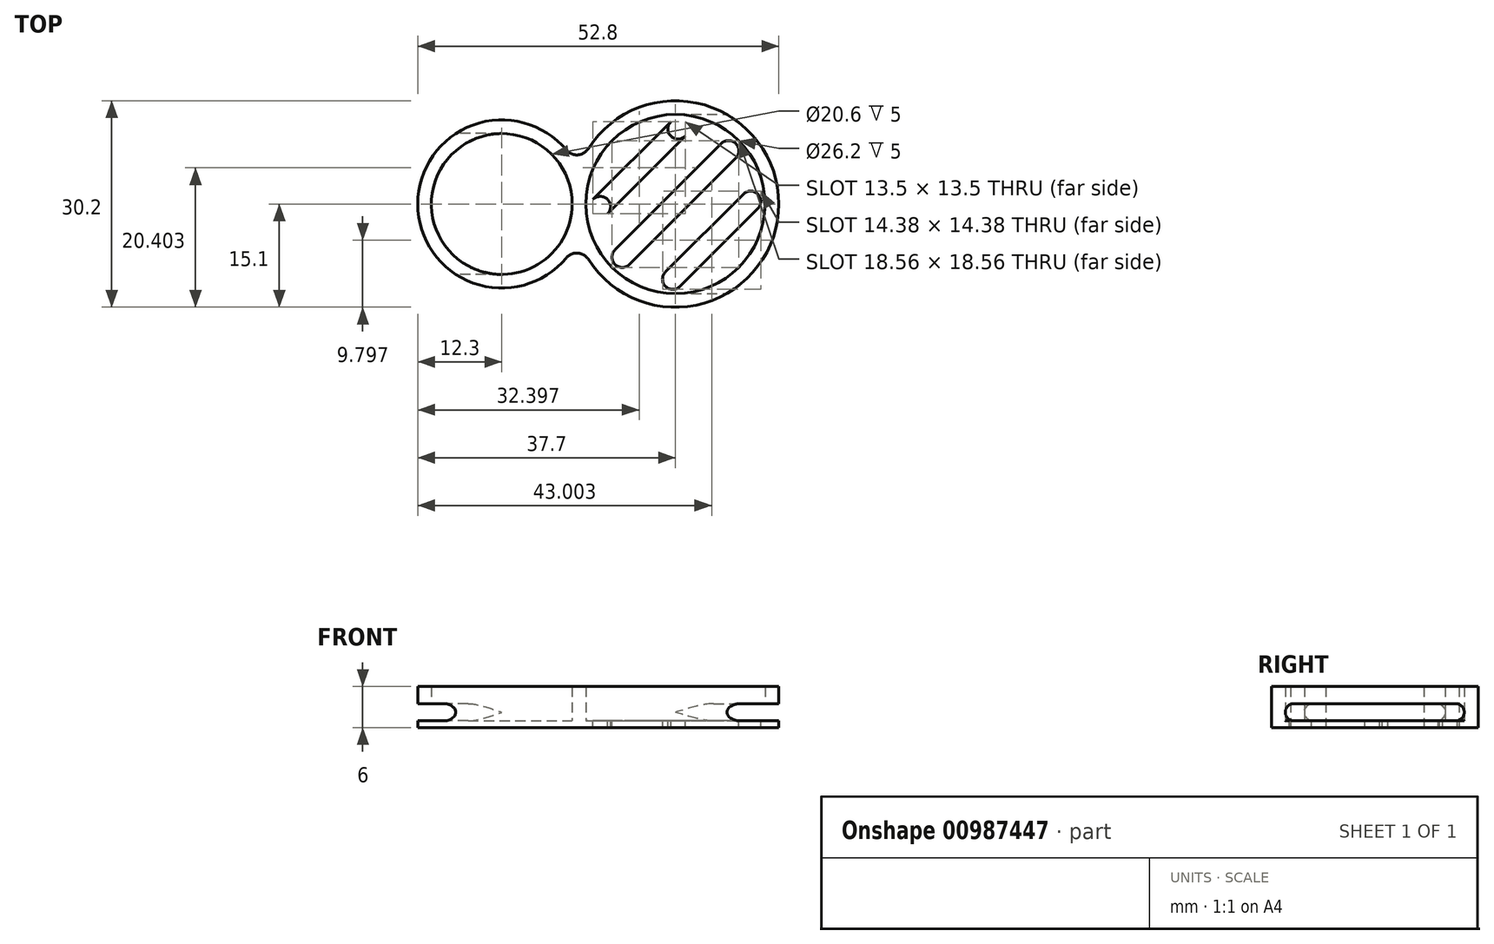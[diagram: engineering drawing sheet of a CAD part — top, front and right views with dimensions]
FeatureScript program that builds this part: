
annotation { "Feature Type Name" : "Feature", "Feature Type Description" : "" }
export const myFeature = defineFeature(function(context is Context, id is Id, definition is map)
    precondition{}
    {
        {
            var Q0;
            Q0=qCreatedBy(makeId("Top.planeOp"),FACE);
            var sketch = newSketch(context, id + "F0", { "sketchPlane" : qUnion([Q0])});
            skCircle(sketch, "E0", {"center": v(-11.3, 0) * mm, "radius": 10.3 * mm});
            skCircle(sketch, "E1", {"center": v(14.1, 0) * mm, "radius": 13.1 * mm});
            skArc(sketch, "E2", {"start": v(1.36, -8.1) * mm, "mid": v(29.2, 0) * mm, "end": v(1.36, 8.1) * mm});
            skArc(sketch, "E3", {"start": v(-1.86, 7.9) * mm, "mid": v(-23.6, 0) * mm, "end": v(-1.86, -7.9) * mm});
            skPoint(sketch, "E4.visualSharp", {"position": v(-0.11, -5.1) * mm});
            skArc(sketch, "E4.filletArc", {"start": v(1.36, -8.1) * mm, "mid": v(-0.2, -7.18) * mm, "end": v(-1.86, -7.9) * mm});
            skPoint(sketch, "E5.visualSharp", {"position": v(-0.11, 5.1) * mm});
            skArc(sketch, "E5.filletArc", {"start": v(-1.86, 7.9) * mm, "mid": v(-0.2, 7.18) * mm, "end": v(1.36, 8.1) * mm});
            skSolve(sketch);
        }
        {
            var Q0;
            Q0 = qSketchRegion(id + "F0", true);
            var Q1;
            Q1=makeQuery(id+"F0.imprint","IMPRINT",FACE,{"disambiguationData":[TD([[makeQuery(id+"F0.imprint","IMPRINT",EDGE,{"derivedFrom":sQuery(id+"F0.wireOp",EDGE,"E0")}),1.0]])]});
            var Q2;
            Q2=makeQuery(id+"F0.imprint","IMPRINT",FACE,{"disambiguationData":[TD([[makeQuery(id+"F0.imprint","IMPRINT",EDGE,{"derivedFrom":sQuery(id+"F0.wireOp",EDGE,"E1")}),1.0]])]});
            extrude(context, id + "F1", {"entities" : qUnion([Q0, Q1, Q2]), "depth" : 1 * mm, "offsetDistance" : 25 * mm});
        }
        {
            var Q0;
            Q0=makeQuery(id+"F0.imprint","IMPRINT",FACE,{"disambiguationData":[TD([[makeQuery(id+"F0.imprint","IMPRINT",EDGE,{"derivedFrom":sQuery(id+"F0.wireOp",EDGE,"E0")}),-1.0]])]});
            extrude(context, id + "F2", {"entities" : qUnion([Q0]), "operationType" : NewBodyOperationType.ADD, "depth" : 6 * mm, "offsetDistance" : 25 * mm});
        }
        {
            var Q0;
            Q0=qCreatedBy(makeId("Right.planeOp"),FACE);
            cPlane(context, id + "F3", {"entities" : qUnion([Q0]), "cplaneType" : CPlaneType.OFFSET, "offset" : 40 * mm, "oppositeDirection" : true, "width" : 150 * mm, "height" : 150 * mm});
        }
        {
            var Q0;
            Q0=qCreatedBy(id+"F3.planeOp",FACE);
            var sketch = newSketch(context, id + "F4", { "sketchPlane" : qUnion([Q0])});
            skLineSegment(sketch, "E6.bottom", {"start": v(9.05, 3.5) * mm, "end": v(-9.05, 3.5) * mm});
            skLineSegment(sketch, "E6.top", {"start": v(9.05, 1) * mm, "end": v(-9.05, 1) * mm});
            skLineSegment(sketch, "E6.left", {"start": v(10.3, 2.25) * mm, "end": v(10.3, 2.25) * mm});
            skLineSegment(sketch, "E6.right", {"start": v(-10.3, 2.25) * mm, "end": v(-10.3, 2.25) * mm});
            skLineSegment(sketch, "E7", {"start": v(0, 1) * mm, "end": v(0, 0) * mm, "construction": true});
            skPoint(sketch, "E8.visualSharp", {"position": v(10.3, 3.5) * mm});
            skArc(sketch, "E8.filletArc", {"start": v(10.3, 2.25) * mm, "mid": v(9.93, 3.13) * mm, "end": v(9.05, 3.5) * mm});
            skPoint(sketch, "E9.visualSharp", {"position": v(10.3, 1) * mm});
            skArc(sketch, "E9.filletArc", {"start": v(9.05, 1) * mm, "mid": v(9.93, 1.37) * mm, "end": v(10.3, 2.25) * mm});
            skPoint(sketch, "E10.visualSharp", {"position": v(-10.3, 1) * mm});
            skArc(sketch, "E10.filletArc", {"start": v(-10.3, 2.25) * mm, "mid": v(-9.93, 1.37) * mm, "end": v(-9.05, 1) * mm});
            skPoint(sketch, "E11.visualSharp", {"position": v(-10.3, 3.5) * mm});
            skArc(sketch, "E11.filletArc", {"start": v(-9.05, 3.5) * mm, "mid": v(-9.93, 3.13) * mm, "end": v(-10.3, 2.25) * mm});
            skSolve(sketch);
        }
        {
            var Q0;
            Q0 = qSketchRegion(id + "F4", true);
            extrude(context, id + "F5", {"entities" : qUnion([Q0]), "operationType" : NewBodyOperationType.REMOVE, "depth" : 28.7 * mm, "offsetDistance" : 25 * mm});
        }
        {
            var Q0;
            Q0=qCreatedBy(makeId("Right.planeOp"),FACE);
            cPlane(context, id + "F6", {"entities" : qUnion([Q0]), "cplaneType" : CPlaneType.OFFSET, "offset" : 40 * mm, "width" : 150 * mm, "height" : 150 * mm});
        }
        {
            var Q0;
            Q0=qCreatedBy(id+"F6.planeOp",FACE);
            var sketch = newSketch(context, id + "F7", { "sketchPlane" : qUnion([Q0])});
            skLineSegment(sketch, "E12.bottom", {"start": v(-11.85, 3.5) * mm, "end": v(11.85, 3.5) * mm});
            skLineSegment(sketch, "E12.top", {"start": v(-11.85, 1) * mm, "end": v(11.85, 1) * mm});
            skLineSegment(sketch, "E12.left", {"start": v(-13.1, 2.25) * mm, "end": v(-13.1, 2.25) * mm});
            skLineSegment(sketch, "E12.right", {"start": v(13.1, 2.25) * mm, "end": v(13.1, 2.25) * mm});
            skLineSegment(sketch, "E13", {"start": v(0, 1) * mm, "end": v(0, 0) * mm, "construction": true});
            skPoint(sketch, "E14.visualSharp", {"position": v(13.1, 1) * mm});
            skArc(sketch, "E14.filletArc", {"start": v(11.85, 1) * mm, "mid": v(12.73, 1.37) * mm, "end": v(13.1, 2.25) * mm});
            skPoint(sketch, "E15.visualSharp", {"position": v(13.1, 3.5) * mm});
            skArc(sketch, "E15.filletArc", {"start": v(13.1, 2.25) * mm, "mid": v(12.73, 3.13) * mm, "end": v(11.85, 3.5) * mm});
            skPoint(sketch, "E16.visualSharp", {"position": v(-13.1, 1) * mm});
            skArc(sketch, "E16.filletArc", {"start": v(-13.1, 2.25) * mm, "mid": v(-12.73, 1.37) * mm, "end": v(-11.85, 1) * mm});
            skPoint(sketch, "E17.visualSharp", {"position": v(-13.1, 3.5) * mm});
            skArc(sketch, "E17.filletArc", {"start": v(-11.85, 3.5) * mm, "mid": v(-12.73, 3.13) * mm, "end": v(-13.1, 2.25) * mm});
            skSolve(sketch);
        }
        {
            var Q0;
            Q0 = qSketchRegion(id + "F7", true);
            extrude(context, id + "F8", {"entities" : qUnion([Q0]), "operationType" : NewBodyOperationType.REMOVE, "oppositeDirection" : true, "depth" : 25.9 * mm, "offsetDistance" : 25 * mm});
        }
        {
            var Q0;
            Q0=makeQuery(id+"F8.boolean.opBoolean","MERGE",FACE,{"derivedFrom":[makeQuery(id+"F2.boolean.opBoolean","SPLIT",FACE,{"disambiguationData":[TD([makeQuery(id+"F2.opExtrude","SWEPT_FACE",FACE,{"disambiguationData":[OSD([sQuery(id+"F0.wireOp",EDGE,"E1")])]})])],"derivedFrom":makeQuery(id+"F1.opExtrude","CAP_FACE",FACE,{"disambiguationData":[OSD([sQuery(id+"F0.wireOp",EDGE,"E2"),sQuery(id+"F0.wireOp",EDGE,"E3"),sQuery(id+"F0.wireOp",EDGE,"E4.filletArc"),sQuery(id+"F0.wireOp",EDGE,"E5.filletArc")])],"isStart":false})})],"fromTools":[makeQuery(id+"F8.opExtrude","SWEPT_FACE",FACE,{"disambiguationData":[OSD([sQuery(id+"F7.wireOp",EDGE,"E12.top")])]})]});
            var sketch = newSketch(context, id + "F9", { "sketchPlane" : qUnion([Q0])});
            skCircle(sketch, "E18", {"center": v(14.1, 0) * mm, "radius": 12.5 * mm});
            skLineSegment(sketch, "E19", {"start": v(5.26, -8.84) * mm, "end": v(22.94, 8.84) * mm, "construction": true});
            skLineSegment(sketch, "E20", {"start": v(14.1, 12.5) * mm, "end": v(14.1, -12.5) * mm, "construction": true});
            skLineSegment(sketch, "E21", {"start": v(5.26, -6.72) * mm, "end": v(20.82, 8.84) * mm});
            skLineSegment(sketch, "E22", {"start": v(22.94, 8.84) * mm, "end": v(22.94, 8.84) * mm});
            skLineSegment(sketch, "E23", {"start": v(22.94, 6.72) * mm, "end": v(7.38, -8.84) * mm});
            skLineSegment(sketch, "E24", {"start": v(5.26, -8.84) * mm, "end": v(5.26, -8.84) * mm});
            skLineSegment(sketch, "E25", {"start": v(13.04, 1.06) * mm, "end": v(14.1, 0) * mm});
            skPoint(sketch, "E26.visualSharp", {"position": v(24, 7.78) * mm});
            skArc(sketch, "E26.filletArc", {"start": v(22.94, 6.72) * mm, "mid": v(23.38, 7.78) * mm, "end": v(22.94, 8.84) * mm});
            skPoint(sketch, "E27.visualSharp", {"position": v(21.88, 9.9) * mm});
            skArc(sketch, "E27.filletArc", {"start": v(22.94, 8.84) * mm, "mid": v(21.88, 9.28) * mm, "end": v(20.82, 8.84) * mm});
            skPoint(sketch, "E28.visualSharp", {"position": v(6.32, -9.9) * mm});
            skArc(sketch, "E28.filletArc", {"start": v(5.26, -8.84) * mm, "mid": v(6.32, -9.28) * mm, "end": v(7.38, -8.84) * mm});
            skPoint(sketch, "E29.visualSharp", {"position": v(4.2, -7.78) * mm});
            skArc(sketch, "E29.filletArc", {"start": v(5.26, -6.72) * mm, "mid": v(4.82, -7.78) * mm, "end": v(5.26, -8.84) * mm});
            skLineSegment(sketch, "E30", {"start": v(12.33, -12.37) * mm, "end": v(26.47, 1.77) * mm, "construction": true});
            skLineSegment(sketch, "E31", {"start": v(24.03, 1.45) * mm, "end": v(12.65, -9.93) * mm});
            skLineSegment(sketch, "E32", {"start": v(14.77, -12.05) * mm, "end": v(26.15, -0.67) * mm});
            skLineSegment(sketch, "E33", {"start": v(18.34, -4.24) * mm, "end": v(5.26, 8.84) * mm, "construction": true});
            skCircle(sketch, "E34", {"center": v(25.1, 0.39) * mm, "radius": 1.5 * mm});
            skCircle(sketch, "E35", {"center": v(13.71, -11) * mm, "radius": 1.5 * mm});
            skPoint(sketch, "E36.orphan", {"position": v(26.3, 3.71) * mm});
            skPoint(sketch, "E37.start.orphan", {"position": v(10.39, -12.2) * mm});
            skLineSegment(sketch, "E38.MirrorCS", {"start": v(15.55, 9.93) * mm, "end": v(4.17, -1.45) * mm});
            skCircle(sketch, "E39.MirrorC", {"center": v(3.1, -0.39) * mm, "radius": 1.5 * mm});
            skLineSegment(sketch, "E40.MirrorCS", {"start": v(2.05, 0.67) * mm, "end": v(13.43, 12.05) * mm});
            skCircle(sketch, "E41.MirrorC", {"center": v(14.49, 11) * mm, "radius": 1.5 * mm});
            skSolve(sketch);
        }
        {
            var Q0;
            {var subQ0=sQuery(id+"F9.wireOp",EDGE,"E38.MirrorCS");Q0=makeQuery(id+"F9.imprint","IMPRINT",FACE,{"disambiguationData":[TD([[makeQuery(id+"F9.imprint","IMPRINT",EDGE,{"derivedFrom":subQ0}),-1.0]])]});}
            var Q1;
            {var subQ0=sQuery(id+"F9.wireOp",EDGE,"E41.MirrorC");var subQ1=makeQuery(id+"F9.imprint","INTERSECT",VERTEX,{"derivedFrom":[sQuery(id+"F9.wireOp",EDGE,"E38.MirrorCS"),subQ0]});Q1=makeQuery(id+"F9.imprint","IMPRINT",FACE,{"disambiguationData":[TD([[makeQuery(id+"F9.imprint","IMPRINT",EDGE,{"disambiguationData":[TD([[subQ1,1.0]])],"derivedFrom":subQ0}),-1.0]])]});}
            var Q2;
            {var subQ0=sQuery(id+"F9.wireOp",EDGE,"E39.MirrorC");var subQ1=makeQuery(id+"F9.imprint","INTERSECT",VERTEX,{"derivedFrom":[sQuery(id+"F9.wireOp",EDGE,"E38.MirrorCS"),subQ0]});Q2=makeQuery(id+"F9.imprint","IMPRINT",FACE,{"disambiguationData":[TD([[makeQuery(id+"F9.imprint","IMPRINT",EDGE,{"disambiguationData":[TD([[subQ1,-1.0]])],"derivedFrom":subQ0}),-1.0]])]});}
            var Q3;
            Q3=makeQuery(id+"F9.imprint","IMPRINT",FACE,{"disambiguationData":[TD([[makeQuery(id+"F9.imprint","IMPRINT",EDGE,{"derivedFrom":sQuery(id+"F9.wireOp",EDGE,"E23")}),-1.0]])]});
            var Q4;
            {var subQ0=sQuery(id+"F9.wireOp",EDGE,"E31");Q4=makeQuery(id+"F9.imprint","IMPRINT",FACE,{"disambiguationData":[TD([[makeQuery(id+"F9.imprint","IMPRINT",EDGE,{"derivedFrom":subQ0}),1.0]])]});}
            var Q5;
            {var subQ0=sQuery(id+"F9.wireOp",EDGE,"E35");var subQ1=makeQuery(id+"F9.imprint","INTERSECT",VERTEX,{"derivedFrom":[sQuery(id+"F9.wireOp",EDGE,"E31"),subQ0]});Q5=makeQuery(id+"F9.imprint","IMPRINT",FACE,{"disambiguationData":[TD([[makeQuery(id+"F9.imprint","IMPRINT",EDGE,{"disambiguationData":[TD([[subQ1,-1.0]])],"derivedFrom":subQ0}),1.0]])]});}
            var Q6;
            {var subQ0=sQuery(id+"F9.wireOp",EDGE,"E34");var subQ1=makeQuery(id+"F9.imprint","INTERSECT",VERTEX,{"derivedFrom":[sQuery(id+"F9.wireOp",EDGE,"E31"),subQ0]});Q6=makeQuery(id+"F9.imprint","IMPRINT",FACE,{"disambiguationData":[TD([[makeQuery(id+"F9.imprint","IMPRINT",EDGE,{"disambiguationData":[TD([[subQ1,1.0]])],"derivedFrom":subQ0}),1.0]])]});}
            extrude(context, id + "F10", {"entities" : qUnion([Q0, Q1, Q2, Q3, Q4, Q5, Q6]), "operationType" : NewBodyOperationType.REMOVE, "oppositeDirection" : true, "depth" : 25 * mm, "offsetDistance" : 25 * mm});
        }
    });
